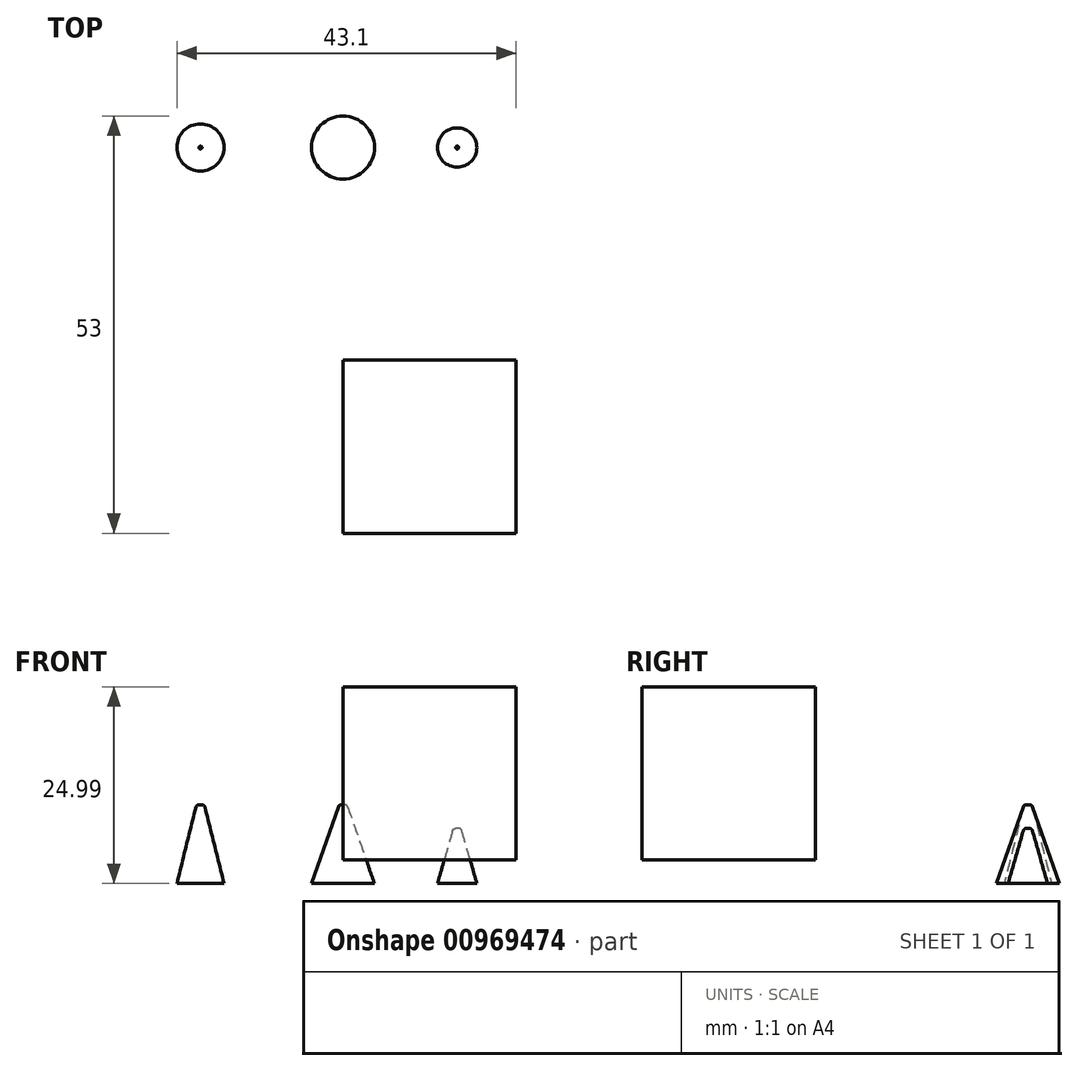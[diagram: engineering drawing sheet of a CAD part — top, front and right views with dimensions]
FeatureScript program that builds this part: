
annotation { "Feature Type Name" : "Feature", "Feature Type Description" : "" }
export const myFeature = defineFeature(function(context is Context, id is Id, definition is map)
    precondition{}
    {
        {
            var Q0;
            Q0=qCreatedBy(makeId("Top.planeOp"),FACE);
            var sketch = newSketch(context, id + "F0", { "sketchPlane" : qUnion([Q0])});
            skCircle(sketch, "E0", {"center": v(0, 0) * mm, "radius": 4 * mm});
            skLineSegment(sketch, "E1", {"start": v(0, 0) * mm, "end": v(4, 0) * mm});
            skCircle(sketch, "E2", {"center": v(-18.1, 0) * mm, "radius": 3 * mm});
            skCircle(sketch, "E3", {"center": v(14.5, 0) * mm, "radius": 2.5 * mm});
            skSolve(sketch);
        }
        {
            var Q0;
            Q0=qCreatedBy(makeId("Top.planeOp"),FACE);
            cPlane(context, id + "F1", {"entities" : qUnion([Q0]), "cplaneType" : CPlaneType.OFFSET, "offset" : 7 * mm, "width" : 150 * mm, "height" : 150 * mm});
        }
        {
            var Q0;
            Q0=qCreatedBy(makeId("Top.planeOp"),FACE);
            cPlane(context, id + "F2", {"entities" : qUnion([Q0]), "cplaneType" : CPlaneType.OFFSET, "offset" : 10 * mm, "width" : 150 * mm, "height" : 150 * mm});
        }
        {
            var Q0;
            Q0=qCreatedBy(id+"F1.planeOp",FACE);
            var sketch = newSketch(context, id + "F3", { "sketchPlane" : qUnion([Q0])});
            skCircle(sketch, "E4", {"center": v(14.51, 0) * mm, "radius": 0.5 * mm});
            skSolve(sketch);
        }
        {
            var Q0;
            Q0=qCreatedBy(id+"F2.planeOp",FACE);
            var sketch = newSketch(context, id + "F4", { "sketchPlane" : qUnion([Q0])});
            skCircle(sketch, "E5", {"center": v(0, 0) * mm, "radius": 0.5 * mm});
            skCircle(sketch, "E6", {"center": v(-18.1, 0) * mm, "radius": 0.5 * mm});
            skSolve(sketch);
        }
        {
            var Q0;
            Q0=makeQuery(id+"F0.imprint","IMPRINT",FACE,{"disambiguationData":[TD([[makeQuery(id+"F0.imprint","IMPRINT",EDGE,{"derivedFrom":sQuery(id+"F0.wireOp",EDGE,"E0")}),1.0]])]});
            var Q1;
            Q1=makeQuery(id+"F4.imprint","IMPRINT",FACE,{"disambiguationData":[TD([[makeQuery(id+"F4.imprint","IMPRINT",EDGE,{"derivedFrom":sQuery(id+"F4.wireOp",EDGE,"E5")}),1.0]])]});
            loft(context, id + "F5", {"sheetProfilesArray" : [{ "sheetProfileEntities" : qUnion([Q0]) }, { "sheetProfileEntities" : qUnion([Q1]) }]});
        }
        {
            var Q0;
            Q0=makeQuery(id+"F0.imprint","IMPRINT",FACE,{"disambiguationData":[TD([[makeQuery(id+"F0.imprint","IMPRINT",EDGE,{"derivedFrom":sQuery(id+"F0.wireOp",EDGE,"E2")}),1.0]])]});
            var Q1;
            Q1=makeQuery(id+"F4.imprint","IMPRINT",FACE,{"disambiguationData":[TD([[makeQuery(id+"F4.imprint","IMPRINT",EDGE,{"derivedFrom":sQuery(id+"F4.wireOp",EDGE,"E6")}),1.0]])]});
            loft(context, id + "F6", {"sheetProfilesArray" : [{ "sheetProfileEntities" : qUnion([Q0]) }, { "sheetProfileEntities" : qUnion([Q1]) }]});
        }
        {
            var Q0;
            Q0=makeQuery(id+"F0.imprint","IMPRINT",FACE,{"disambiguationData":[TD([[makeQuery(id+"F0.imprint","IMPRINT",EDGE,{"derivedFrom":sQuery(id+"F0.wireOp",EDGE,"E3")}),1.0]])]});
            var Q1;
            Q1=makeQuery(id+"F3.imprint","IMPRINT",FACE,{"disambiguationData":[TD([[makeQuery(id+"F3.imprint","IMPRINT",EDGE,{"derivedFrom":sQuery(id+"F3.wireOp",EDGE,"E4")}),1.0]])]});
            loft(context, id + "F7", {"sheetProfilesArray" : [{ "sheetProfileEntities" : qUnion([Q0]) }, { "sheetProfileEntities" : qUnion([Q1]) }]});
        }
        {
            var Q0;
            Q0=makeQuery(id+"F5.opLoft","MID_CAP_EDGE",EDGE,{"disambiguationData":[OSD([sQuery(id+"F4.wireOp",EDGE,"E5")])],"capPos":1.0});
            var Q1;
            Q1=makeQuery(id+"F6.opLoft","MID_CAP_EDGE",EDGE,{"disambiguationData":[OSD([sQuery(id+"F4.wireOp",EDGE,"E6")])],"capPos":1.0});
            var Q2;
            Q2=makeQuery(id+"F7.opLoft","MID_CAP_EDGE",EDGE,{"disambiguationData":[OSD([sQuery(id+"F3.wireOp",EDGE,"E4")])],"capPos":1.0});
            fillet(context, id + "F8", {"entities" : qUnion([Q0, Q1, Q2]), "tangentPropagation" : true, "radius" : .4 * mm, "defaultsChanged" : false, "vertexSettings" : [], "allowEdgeOverflow" : false});
        }
        {
            var Q0;
            Q0=qCreatedBy(makeId("Right.planeOp"),FACE);
            var sketch = newSketch(context, id + "F9", { "sketchPlane" : qUnion([Q0])});
            skLineSegment(sketch, "E7.bottom", {"start": v(-49, 24.99) * mm, "end": v(-27, 24.99) * mm});
            skLineSegment(sketch, "E7.top", {"start": v(-49, 2.99) * mm, "end": v(-27, 2.99) * mm});
            skLineSegment(sketch, "E7.left", {"start": v(-49, 24.99) * mm, "end": v(-49, 2.99) * mm});
            skLineSegment(sketch, "E7.right", {"start": v(-27, 24.99) * mm, "end": v(-27, 2.99) * mm});
            skSolve(sketch);
        }
        {
            var Q0;
            Q0=makeQuery(id+"F9.imprint","IMPRINT",FACE,{"disambiguationData":[TD([[makeQuery(id+"F9.imprint","IMPRINT",EDGE,{"derivedFrom":sQuery(id+"F9.wireOp",EDGE,"E7.bottom")}),-1.0]])]});
            extrude(context, id + "F10", {"entities" : qUnion([Q0]), "depth" : 22 * mm, "offsetDistance" : 25 * mm});
        }
    });
